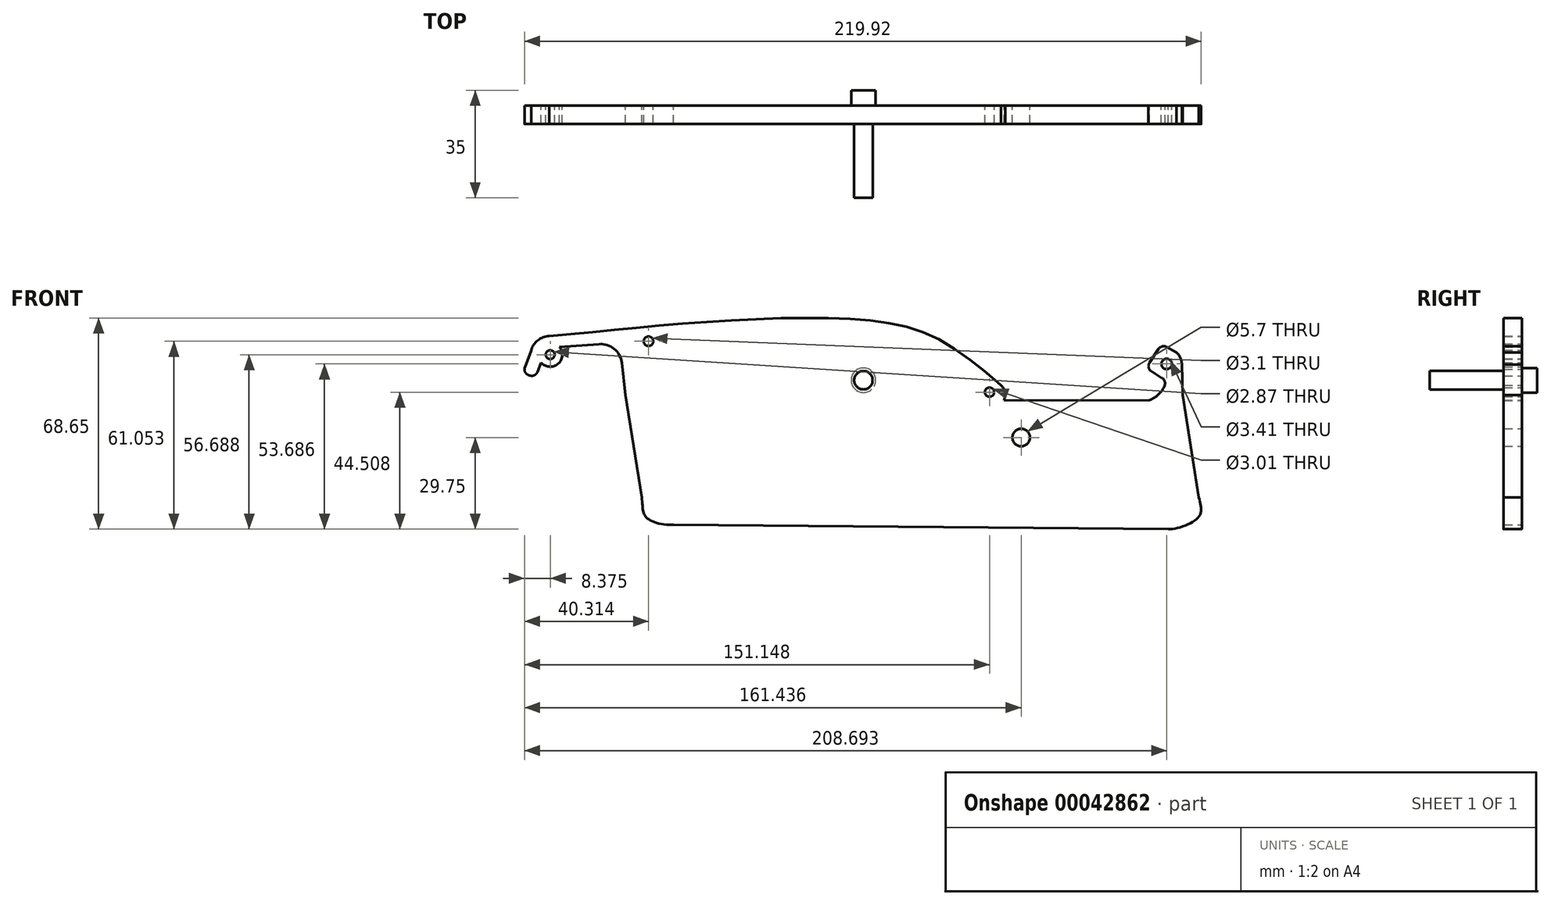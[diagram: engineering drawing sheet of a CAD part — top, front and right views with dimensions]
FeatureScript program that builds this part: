
annotation { "Feature Type Name" : "Feature", "Feature Type Description" : "" }
export const myFeature = defineFeature(function(context is Context, id is Id, definition is map)
    precondition{}
    {
        {
            var Q0;
            Q0=qCreatedBy(makeId("Front.planeOp"),FACE);
            var sketch = newSketch(context, id + "F0", { "sketchPlane" : qUnion([Q0])});
            skCircle(sketch, "E0", {"center": v(-73.72, 35.16) * mm, "radius": 1.44 * mm});
            skCircle(sketch, "E1", {"center": v(-41.78, 39.52) * mm, "radius": 1.55 * mm});
            skCircle(sketch, "E2", {"center": v(28.07, 26.86) * mm, "radius": 2.97 * mm});
            skCircle(sketch, "E3", {"center": v(79.35, 8.22) * mm, "radius": 2.85 * mm});
            skCircle(sketch, "E4", {"center": v(69.06, 22.98) * mm, "radius": 1.5 * mm});
            skCircle(sketch, "E5", {"center": v(126.6, 32.16) * mm, "radius": 1.7 * mm});
            skFitSpline(sketch, "E6", {"points": [v(-74.03, 41.2) * mm, v(-26.74, 45.56) * mm, v(26.59, 46.59) * mm, v(55.72, 38.33) * mm, v(72.81, 25.2) * mm], "startDerivative": vector(161.35, 14.36) * mm, "endDerivative": vector(26.37, -21.19) * mm});
            skLineSegment(sketch, "E7", {"start": v(73.72, 20.3) * mm, "end": v(121.03, 20.38) * mm});
            skFitSpline(sketch, "E8", {"points": [v(73.75, 17.77) * mm, v(123.46, 21.8) * mm, v(126.45, 31.99) * mm], "startDerivative": vector(8.74, 2.96) * mm, "endDerivative": vector(0.7, 5.97) * mm});
            skLineSegment(sketch, "E9", {"start": v(126.42, 26.74) * mm, "end": v(119.92, 30.82) * mm});
            skLineSegment(sketch, "E10", {"start": v(119.92, 30.82) * mm, "end": v(125, 38.61) * mm});
            skLineSegment(sketch, "E11", {"start": v(129.76, 35.92) * mm, "end": v(125, 38.61) * mm});
            skLineSegment(sketch, "E12", {"start": v(131.51, 31.99) * mm, "end": v(131.85, 22) * mm});
            skLineSegment(sketch, "E13", {"start": v(131.85, 22) * mm, "end": v(137.1, -11.2) * mm});
            skLineSegment(sketch, "E14", {"start": v(-49.22, 22) * mm, "end": v(-51.2, 39.1) * mm});
            skLineSegment(sketch, "E15", {"start": v(-82.66, 29.24) * mm, "end": v(-79.94, 36.56) * mm});
            skLineSegment(sketch, "E16", {"start": v(-82.66, 29.24) * mm, "end": v(-78.55, 27.7) * mm});
            skLineSegment(sketch, "E17", {"start": v(-78.55, 27.7) * mm, "end": v(-76.71, 32.64) * mm});
            skArc(sketch, "E18", {"start": v(131.51, 31.99) * mm, "mid": v(131.1, 34.16) * mm, "end": v(129.76, 35.92) * mm});
            skArc(sketch, "E19", {"start": v(73.72, 20.3) * mm, "mid": v(74.06, 22.9) * mm, "end": v(72.8, 25.22) * mm});
            skArc(sketch, "E20", {"start": v(-74.03, 41.2) * mm, "mid": v(-77.74, 39.84) * mm, "end": v(-79.94, 36.56) * mm});
            skArc(sketch, "E21", {"start": v(-76.71, 32.64) * mm, "mid": v(-71.2, 32.16) * mm, "end": v(-70.72, 37.68) * mm});
            skLineSegment(sketch, "E22", {"start": v(-70.72, 37.68) * mm, "end": v(-51.2, 39.1) * mm});
            skLineSegment(sketch, "E23", {"start": v(-43.96, -11.2) * mm, "end": v(-49.22, 22) * mm});
            skLineSegment(sketch, "E24", {"start": v(-43.96, -11.2) * mm, "end": v(-43.96, 44.8) * mm, "construction": true});
            skLineSegment(sketch, "E25", {"start": v(137.1, -11.2) * mm, "end": v(137.1, 48.48) * mm, "construction": true});
            skLineSegment(sketch, "E26", {"start": v(-43.96, -11.2) * mm, "end": v(169, -11.2) * mm, "construction": true});
            skFitSpline(sketch, "E27", {"points": [v(-43.96, -11.2) * mm, v(-42.05, -18.13) * mm, v(-26.98, -18.64) * mm], "startDerivative": vector(2.62, -23.53) * mm, "endDerivative": vector(24.61, 12.27) * mm});
            skFitSpline(sketch, "E28", {"points": [v(137.1, -11.2) * mm, v(137.1, -17.46) * mm, v(127.28, -21.52) * mm, v(121.86, -19.32) * mm], "startDerivative": vector(5.76, -24.62) * mm, "endDerivative": vector(-20.78, 9.71) * mm});
            skLineSegment(sketch, "E29", {"start": v(-35.08, -20.13) * mm, "end": v(127.78, -21.52) * mm});
            skSolve(sketch);
        }
        {
            var Q0;
            Q0 = qSketchRegion(id + "F0", true);
            extrude(context, id + "F1", {"entities" : qUnion([Q0]), "depth" : 6 * mm});
        }
        {
            var Q0;
            Q0=makeQuery(id+"F1.opExtrude","SWEPT_EDGE",EDGE,{"disambiguationData":[OSD([sQuery(id+"F0.wireOp",EDGE,"E14"),sQuery(id+"F0.wireOp",EDGE,"E22")])]});
            fillet(context, id + "F2", {"entities" : qUnion([Q0]), "radius" : 7 * mm, "tangentPropagation" : true, "allowEdgeOverflow" : false});
        }
        {
            var Q0;
            Q0=makeQuery(id+"F1.opExtrude","SWEPT_EDGE",EDGE,{"disambiguationData":[OSD([sQuery(id+"F0.wireOp",EDGE,"E15"),sQuery(id+"F0.wireOp",EDGE,"E16")])]});
            var Q1;
            Q1=makeQuery(id+"F1.opExtrude","SWEPT_EDGE",EDGE,{"disambiguationData":[OSD([sQuery(id+"F0.wireOp",EDGE,"E16"),sQuery(id+"F0.wireOp",EDGE,"E17")])]});
            var Q2;
            Q2=makeQuery(id+"F1.opExtrude","SWEPT_EDGE",EDGE,{"disambiguationData":[OSD([sQuery(id+"F0.wireOp",EDGE,"E8"),sQuery(id+"F0.wireOp",EDGE,"E9")])]});
            var Q3;
            Q3=makeQuery(id+"F1.opExtrude","SWEPT_EDGE",EDGE,{"disambiguationData":[OSD([sQuery(id+"F0.wireOp",EDGE,"E9"),sQuery(id+"F0.wireOp",EDGE,"E10")])]});
            var Q4;
            Q4=makeQuery(id+"F1.opExtrude","SWEPT_EDGE",EDGE,{"disambiguationData":[OSD([sQuery(id+"F0.wireOp",EDGE,"E10"),sQuery(id+"F0.wireOp",EDGE,"E11")])]});
            fillet(context, id + "F3", {"entities" : qUnion([Q0, Q1, Q2, Q3, Q4]), "radius" : 2 * mm, "tangentPropagation" : true, "allowEdgeOverflow" : false});
        }
        {
            var Q0;
            Q0=makeQuery(id+"F1.opExtrude","CAP_FACE",FACE,{"disambiguationData":[OSD([sQuery(id+"F0.wireOp",EDGE,"E0"),sQuery(id+"F0.wireOp",EDGE,"E1"),sQuery(id+"F0.wireOp",EDGE,"E2"),sQuery(id+"F0.wireOp",EDGE,"E3"),sQuery(id+"F0.wireOp",EDGE,"E4"),sQuery(id+"F0.wireOp",EDGE,"E5"),sQuery(id+"F0.wireOp",EDGE,"E6"),sQuery(id+"F0.wireOp",EDGE,"E7"),sQuery(id+"F0.wireOp",EDGE,"E8"),sQuery(id+"F0.wireOp",EDGE,"E9"),sQuery(id+"F0.wireOp",EDGE,"E10"),sQuery(id+"F0.wireOp",EDGE,"E11"),sQuery(id+"F0.wireOp",EDGE,"E12"),sQuery(id+"F0.wireOp",EDGE,"E13"),sQuery(id+"F0.wireOp",EDGE,"E14"),sQuery(id+"F0.wireOp",EDGE,"E15"),sQuery(id+"F0.wireOp",EDGE,"E16"),sQuery(id+"F0.wireOp",EDGE,"E17"),sQuery(id+"F0.wireOp",EDGE,"E18"),sQuery(id+"F0.wireOp",EDGE,"E19"),sQuery(id+"F0.wireOp",EDGE,"E20"),sQuery(id+"F0.wireOp",EDGE,"E21"),sQuery(id+"F0.wireOp",EDGE,"E22"),sQuery(id+"F0.wireOp",EDGE,"E23"),sQuery(id+"F0.wireOp",EDGE,"E27"),sQuery(id+"F0.wireOp",EDGE,"E28"),sQuery(id+"F0.wireOp",EDGE,"E29")])],"isStart":true});
            var sketch = newSketch(context, id + "F4", { "sketchPlane" : qUnion([Q0])});
            skCircle(sketch, "E30", {"center": v(-28.07, 26.86) * mm, "radius": 4 * mm});
            skSolve(sketch);
        }
        {
            var Q0;
            Q0 = qSketchRegion(id + "F4", true);
            extrude(context, id + "F5", {"entities" : qUnion([Q0]), "depth" : 5 * mm});
        }
        {
            var Q0;
            Q0=makeQuery(id+"F5.opExtrude","CAP_FACE",FACE,{"disambiguationData":[OSD([sQuery(id+"F4.wireOp",EDGE,"E30")])],"isStart":true});
            var sketch = newSketch(context, id + "F6", { "sketchPlane" : qUnion([Q0])});
            skCircle(sketch, "E31", {"center": v(28.07, 26.86) * mm, "radius": 3 * mm});
            skSolve(sketch);
        }
        {
            var Q0;
            Q0 = qSketchRegion(id + "F6", true);
            extrude(context, id + "F7", {"entities" : qUnion([Q0]), "operationType" : NewBodyOperationType.ADD, "depth" : 30 * mm});
        }
    });
